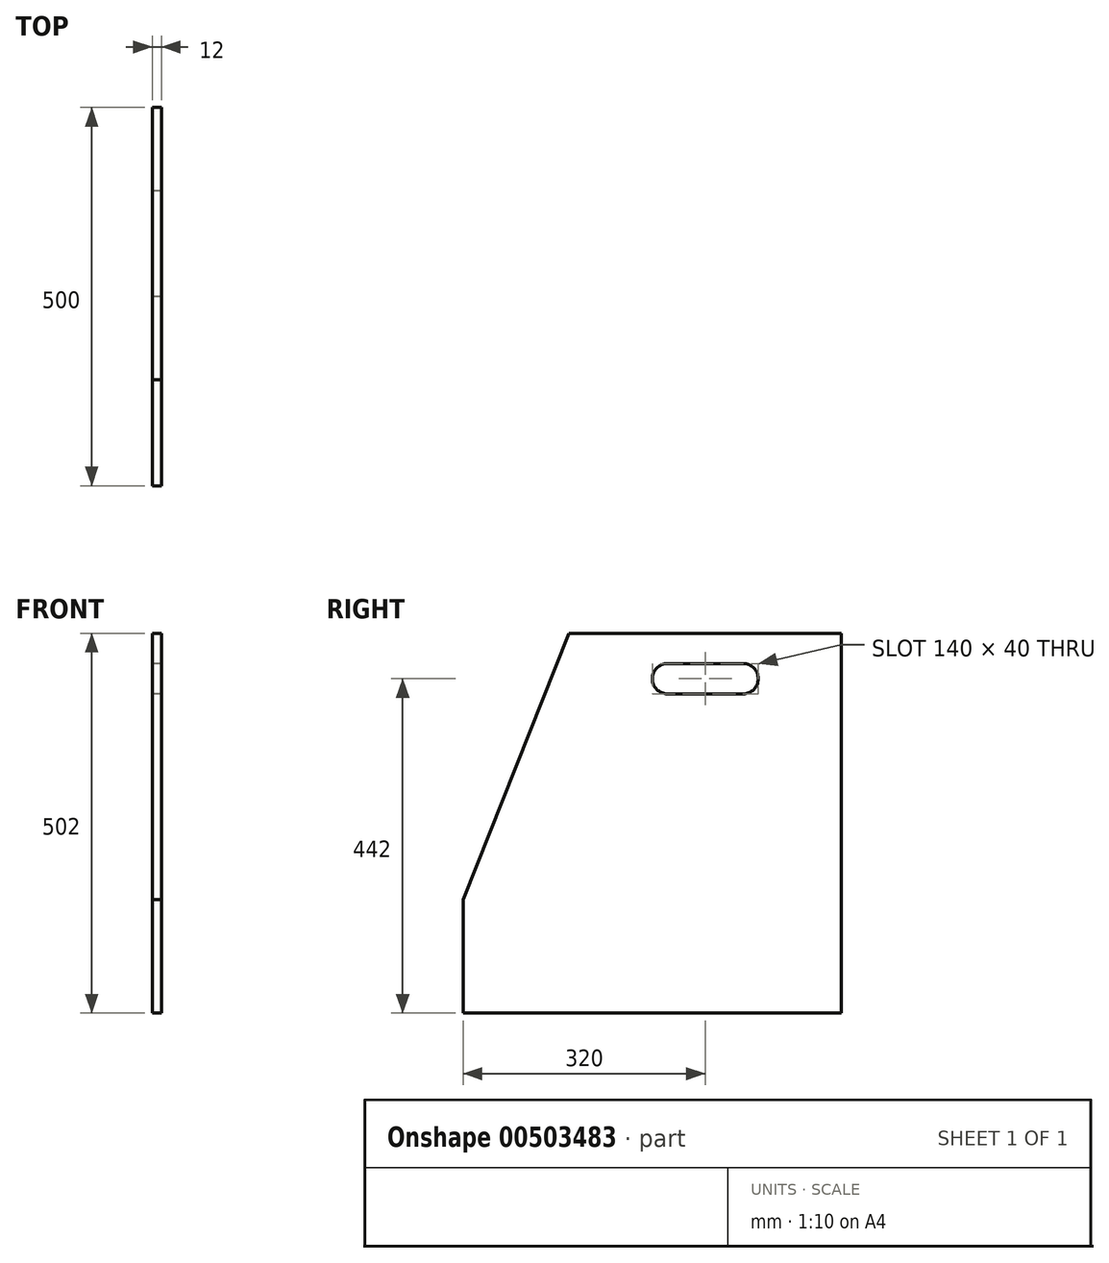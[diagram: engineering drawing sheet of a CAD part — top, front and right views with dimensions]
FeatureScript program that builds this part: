
annotation { "Feature Type Name" : "Feature", "Feature Type Description" : "" }
export const myFeature = defineFeature(function(context is Context, id is Id, definition is map)
    precondition{}
    {
        {
            var Q0;
            Q0=qCreatedBy(makeId("Top.planeOp"),FACE);
            var sketch = newSketch(context, id + "F0", { "sketchPlane" : qUnion([Q0])});
            skLineSegment(sketch, "E0.bottom", {"start": v(250, -250) * mm, "end": v(-250, -250) * mm});
            skLineSegment(sketch, "E0.top", {"start": v(250, 250) * mm, "end": v(-250, 250) * mm});
            skLineSegment(sketch, "E0.left", {"start": v(250, -250) * mm, "end": v(250, 250) * mm});
            skLineSegment(sketch, "E0.right", {"start": v(-250, -250) * mm, "end": v(-250, 250) * mm});
            skPoint(sketch, "E0.middle", {"position": v(0, 0) * mm});
            skSolve(sketch);
        }
        {
            var Q0;
            Q0=qSketchRegion(id+"F0",true);
            extrude(context, id + "F1", {"entities" : qUnion([Q0]), "depth" : 12 * mm, "offsetDistance" : 25 * mm});
        }
        {
            var Q0;
            Q0=qCreatedBy(makeId("Right.planeOp"),FACE);
            var sketch = newSketch(context, id + "F2", { "sketchPlane" : qUnion([Q0])});
            skLineSegment(sketch, "E1.bottom", {"start": v(250, -25) * mm, "end": v(-250, -25) * mm});
            skLineSegment(sketch, "E1.top", {"start": v(250, 25) * mm, "end": v(-250, 25) * mm});
            skLineSegment(sketch, "E1.left", {"start": v(250, -25) * mm, "end": v(250, 25) * mm});
            skLineSegment(sketch, "E1.right", {"start": v(-250, -25) * mm, "end": v(-250, 25) * mm});
            skPoint(sketch, "E1.middle", {"position": v(0, 0) * mm});
            skSolve(sketch);
        }
        {
            var Q0;
            Q0=qSketchRegion(id+"F2",true);
            extrude(context, id + "F3", {"entities" : qUnion([Q0]), "endBound" : BoundingType.SYMMETRIC, "depth" : 12 * mm, "offsetDistance" : 25 * mm});
        }
        {
            var Q0;
            Q0=makeQuery(id+"F3.opExtrude","SWEPT_BODY",BODY,{"disambiguationData":[OSD([sQuery(id+"F2.wireOp",EDGE,"E1.bottom"),sQuery(id+"F2.wireOp",EDGE,"E1.top"),sQuery(id+"F2.wireOp",EDGE,"E1.left"),sQuery(id+"F2.wireOp",EDGE,"E1.right")])]});
            transform(context, id + "F4", {"entities" : qUnion([Q0]), "transformType" : TransformType.TRANSLATION_3D, "dx" : 0 * mm, "dy" : 0 * mm, "dz" : -25 * mm, "makeCopy" : false});
        }
        {
            var Q0;
            Q0=qCreatedBy(makeId("Front.planeOp"),FACE);
            var sketch = newSketch(context, id + "F5", { "sketchPlane" : qUnion([Q0])});
            skLineSegment(sketch, "E2.bottom", {"start": v(250, -25) * mm, "end": v(-250, -25) * mm});
            skLineSegment(sketch, "E2.left", {"start": v(250, -25) * mm, "end": v(250, 25) * mm});
            skLineSegment(sketch, "E2.right", {"start": v(-250, -25) * mm, "end": v(-250, 25) * mm});
            skPoint(sketch, "E2.middle", {"position": v(0, 0) * mm});
            skLineSegment(sketch, "E3", {"start": v(-250, 25) * mm, "end": v(-6, 25) * mm});
            skLineSegment(sketch, "E4", {"start": v(-6, 25) * mm, "end": v(-6, 0) * mm});
            skLineSegment(sketch, "E5", {"start": v(-6, 0) * mm, "end": v(6, 0) * mm});
            skLineSegment(sketch, "E6", {"start": v(6, 0) * mm, "end": v(6, 25) * mm});
            skLineSegment(sketch, "E7", {"start": v(6, 25) * mm, "end": v(250, 25) * mm});
            skSolve(sketch);
        }
        {
            var Q0;
            Q0=qSketchRegion(id+"F5",true);
            extrude(context, id + "F6", {"entities" : qUnion([Q0]), "endBound" : BoundingType.SYMMETRIC, "depth" : 12 * mm, "offsetDistance" : 25 * mm});
        }
        {
            var Q0;
            Q0=makeQuery(id+"F6.opExtrude","SWEPT_BODY",BODY,{"disambiguationData":[OSD([sQuery(id+"F5.wireOp",EDGE,"E2.bottom"),sQuery(id+"F5.wireOp",EDGE,"E2.top"),sQuery(id+"F5.wireOp",EDGE,"E2.left"),sQuery(id+"F5.wireOp",EDGE,"E2.right")])]});
            transform(context, id + "F7", {"entities" : qUnion([Q0]), "transformType" : TransformType.TRANSLATION_3D, "dx" : 0 * mm, "dy" : 80 * mm, "dz" : -25 * mm, "makeCopy" : false});
        }
        {
            var Q0;
            Q0=makeQuery(id+"F6.opExtrude","SWEPT_BODY",BODY,{"disambiguationData":[OSD([sQuery(id+"F5.wireOp",EDGE,"E2.bottom"),sQuery(id+"F5.wireOp",EDGE,"E2.top"),sQuery(id+"F5.wireOp",EDGE,"E2.left"),sQuery(id+"F5.wireOp",EDGE,"E2.right")])]});
            transform(context, id + "F8", {"entities" : qUnion([Q0]), "transformType" : TransformType.COPY});
        }
        {
            var Q0;
            Q0=makeQuery(id+"F8.opPattern","COPY",BODY,{"derivedFrom":makeQuery(id+"F6.opExtrude","SWEPT_BODY",BODY,{"disambiguationData":[OSD([sQuery(id+"F5.wireOp",EDGE,"E2.bottom"),sQuery(id+"F5.wireOp",EDGE,"E2.top"),sQuery(id+"F5.wireOp",EDGE,"E2.left"),sQuery(id+"F5.wireOp",EDGE,"E2.right")])]}),"instanceName":"1"});
            deleteBodies(context, id + "F9", {"entities" : qUnion([Q0])});
        }
        {
            var Q0;
            Q0=makeQuery(id+"F6.opExtrude","SWEPT_BODY",BODY,{"disambiguationData":[OSD([sQuery(id+"F5.wireOp",EDGE,"E2.bottom"),sQuery(id+"F5.wireOp",EDGE,"E2.left"),sQuery(id+"F5.wireOp",EDGE,"E2.right"),sQuery(id+"F5.wireOp",EDGE,"E3"),sQuery(id+"F5.wireOp",EDGE,"E4"),sQuery(id+"F5.wireOp",EDGE,"E5"),sQuery(id+"F5.wireOp",EDGE,"E6"),sQuery(id+"F5.wireOp",EDGE,"E7")])]});
            var Q1;
            Q1=makeQuery(id+"F3.opExtrude","SWEPT_BODY",BODY,{"disambiguationData":[OSD([sQuery(id+"F2.wireOp",EDGE,"E1.bottom"),sQuery(id+"F2.wireOp",EDGE,"E1.top"),sQuery(id+"F2.wireOp",EDGE,"E1.left"),sQuery(id+"F2.wireOp",EDGE,"E1.right")])]});
            booleanBodies(context, id + "F10", {"operationType" : BooleanOperationType.SUBTRACTION, "tools" : qUnion([Q0]), "targets" : qUnion([Q1]), "keepTools" : true});
        }
        {
            var Q0;
            Q0=makeQuery(id+"F6.opExtrude","SWEPT_BODY",BODY,{"disambiguationData":[OSD([sQuery(id+"F5.wireOp",EDGE,"E2.bottom"),sQuery(id+"F5.wireOp",EDGE,"E2.left"),sQuery(id+"F5.wireOp",EDGE,"E2.right"),sQuery(id+"F5.wireOp",EDGE,"E3"),sQuery(id+"F5.wireOp",EDGE,"E4"),sQuery(id+"F5.wireOp",EDGE,"E5"),sQuery(id+"F5.wireOp",EDGE,"E6"),sQuery(id+"F5.wireOp",EDGE,"E7")])]});
            transform(context, id + "F11", {"entities" : qUnion([Q0]), "transformType" : TransformType.TRANSLATION_3D, "dx" : 0 * mm, "dy" : 164 * mm, "dz" : 0 * mm, "makeCopy" : true});
        }
        {
            var Q0;
            Q0=makeQuery(id+"F11.opPattern","COPY",BODY,{"derivedFrom":makeQuery(id+"F6.opExtrude","SWEPT_BODY",BODY,{"disambiguationData":[OSD([sQuery(id+"F5.wireOp",EDGE,"E2.bottom"),sQuery(id+"F5.wireOp",EDGE,"E2.left"),sQuery(id+"F5.wireOp",EDGE,"E2.right"),sQuery(id+"F5.wireOp",EDGE,"E3"),sQuery(id+"F5.wireOp",EDGE,"E4"),sQuery(id+"F5.wireOp",EDGE,"E5"),sQuery(id+"F5.wireOp",EDGE,"E6"),sQuery(id+"F5.wireOp",EDGE,"E7")])]}),"instanceName":"1"});
            var Q1;
            Q1=makeQuery(id+"F3.opExtrude","SWEPT_BODY",BODY,{"disambiguationData":[OSD([sQuery(id+"F2.wireOp",EDGE,"E1.bottom"),sQuery(id+"F2.wireOp",EDGE,"E1.top"),sQuery(id+"F2.wireOp",EDGE,"E1.left"),sQuery(id+"F2.wireOp",EDGE,"E1.right")])]});
            booleanBodies(context, id + "F12", {"operationType" : BooleanOperationType.SUBTRACTION, "tools" : qUnion([Q0]), "targets" : qUnion([Q1]), "keepTools" : true});
        }
        {
            var Q0;
            Q0=qCreatedBy(makeId("Right.planeOp"),FACE);
            var sketch = newSketch(context, id + "F13", { "sketchPlane" : qUnion([Q0])});
            skLineSegment(sketch, "E8", {"start": v(0, 0) * mm, "end": v(250, 0) * mm});
            skLineSegment(sketch, "E9", {"start": v(250, 0) * mm, "end": v(250, -50) * mm});
            skLineSegment(sketch, "E10", {"start": v(250, -50) * mm, "end": v(-250, -50) * mm});
            skLineSegment(sketch, "E11", {"start": v(-250, -50) * mm, "end": v(-250, 100) * mm});
            skLineSegment(sketch, "E12", {"start": v(250, 0) * mm, "end": v(250, 452) * mm});
            skLineSegment(sketch, "E13", {"start": v(250, 452) * mm, "end": v(-110, 452) * mm});
            skLineSegment(sketch, "E14", {"start": v(-110, 452) * mm, "end": v(-250, 100) * mm});
            skLineSegment(sketch, "E15", {"start": v(250, 452) * mm, "end": v(70, 452) * mm});
            skLineSegment(sketch, "E16", {"start": v(70, 452) * mm, "end": v(70, 392) * mm});
            skLineSegment(sketch, "E17.bottom", {"start": v(140, 372) * mm, "end": v(0, 372) * mm});
            skLineSegment(sketch, "E17.top", {"start": v(140, 412) * mm, "end": v(0, 412) * mm});
            skLineSegment(sketch, "E17.left", {"start": v(140, 372) * mm, "end": v(140, 412) * mm});
            skLineSegment(sketch, "E17.right", {"start": v(0, 372) * mm, "end": v(0, 412) * mm});
            skPoint(sketch, "E17.middle", {"position": v(70, 392) * mm});
            skSolve(sketch);
        }
        {
            var Q0;
            Q0=makeQuery(id+"F13.imprint","IMPRINT",FACE,{"disambiguationData":[TD([[makeQuery(id+"F13.imprint","IMPRINT",EDGE,{"derivedFrom":sQuery(id+"F13.wireOp",EDGE,"E9")}),-1.0]])]});
            extrude(context, id + "F14", {"entities" : qUnion([Q0]), "endBound" : BoundingType.SYMMETRIC, "depth" : 12 * mm, "offsetDistance" : 25 * mm});
        }
        {
            var Q0;
            Q0=makeQuery(id+"F14.opExtrude","SWEPT_EDGE",EDGE,{"disambiguationData":[OSD([sQuery(id+"F13.wireOp",EDGE,"E17.bottom"),sQuery(id+"F13.wireOp",EDGE,"E17.left")])]});
            var Q1;
            Q1=makeQuery(id+"F14.opExtrude","SWEPT_EDGE",EDGE,{"disambiguationData":[OSD([sQuery(id+"F13.wireOp",EDGE,"E17.top"),sQuery(id+"F13.wireOp",EDGE,"E17.left")])]});
            var Q2;
            Q2=makeQuery(id+"F14.opExtrude","SWEPT_EDGE",EDGE,{"disambiguationData":[OSD([sQuery(id+"F13.wireOp",EDGE,"E17.top"),sQuery(id+"F13.wireOp",EDGE,"E17.right")])]});
            var Q3;
            Q3=makeQuery(id+"F14.opExtrude","SWEPT_EDGE",EDGE,{"disambiguationData":[OSD([sQuery(id+"F13.wireOp",EDGE,"E17.bottom"),sQuery(id+"F13.wireOp",EDGE,"E17.right")])]});
            fillet(context, id + "F15", {"entities" : qUnion([Q0, Q1, Q2, Q3]), "radius" : 20 * mm, "tangentPropagation" : true, "allowEdgeOverflow" : false});
        }
        {
            var Q0;
            Q0=makeQuery(id+"F14.opExtrude","SWEPT_BODY",BODY,{"disambiguationData":[OSD([sQuery(id+"F13.wireOp",EDGE,"E9"),sQuery(id+"F13.wireOp",EDGE,"E10"),sQuery(id+"F13.wireOp",EDGE,"E11"),sQuery(id+"F13.wireOp",EDGE,"E12"),sQuery(id+"F13.wireOp",EDGE,"E13"),sQuery(id+"F13.wireOp",EDGE,"E14"),sQuery(id+"F13.wireOp",EDGE,"E17.bottom"),sQuery(id+"F13.wireOp",EDGE,"E17.top"),sQuery(id+"F13.wireOp",EDGE,"E17.left"),sQuery(id+"F13.wireOp",EDGE,"E17.right")])]});
            transform(context, id + "F16", {"entities" : qUnion([Q0]), "transformType" : TransformType.TRANSLATION_3D, "dx" : -256 * mm, "dy" : 0 * mm, "dz" : 0 * mm, "makeCopy" : false});
        }
        {
            var Q0;
            Q0=makeQuery(id+"F14.opExtrude","SWEPT_BODY",BODY,{"disambiguationData":[OSD([sQuery(id+"F13.wireOp",EDGE,"E9"),sQuery(id+"F13.wireOp",EDGE,"E10"),sQuery(id+"F13.wireOp",EDGE,"E11"),sQuery(id+"F13.wireOp",EDGE,"E12"),sQuery(id+"F13.wireOp",EDGE,"E13"),sQuery(id+"F13.wireOp",EDGE,"E14"),sQuery(id+"F13.wireOp",EDGE,"E17.bottom"),sQuery(id+"F13.wireOp",EDGE,"E17.top"),sQuery(id+"F13.wireOp",EDGE,"E17.left"),sQuery(id+"F13.wireOp",EDGE,"E17.right")])]});
            transform(context, id + "F17", {"entities" : qUnion([Q0]), "transformType" : TransformType.TRANSLATION_3D, "dx" : 512 * mm, "dy" : 0 * mm, "dz" : 0 * mm, "makeCopy" : true});
        }
        {
            var Q0;
            Q0=qCreatedBy(makeId("Front.planeOp"),FACE);
            var sketch = newSketch(context, id + "F18", { "sketchPlane" : qUnion([Q0])});
            skLineSegment(sketch, "E18", {"start": v(0, 0) * mm, "end": v(-262, 0) * mm});
            skLineSegment(sketch, "E19", {"start": v(-262, 0) * mm, "end": v(-262, -50) * mm});
            skLineSegment(sketch, "E20", {"start": v(-262, -50) * mm, "end": v(262, -50) * mm});
            skLineSegment(sketch, "E21", {"start": v(262, -50) * mm, "end": v(262, 452) * mm});
            skLineSegment(sketch, "E22", {"start": v(262, 452) * mm, "end": v(-262, 452) * mm});
            skLineSegment(sketch, "E23", {"start": v(-262, 452) * mm, "end": v(-262, 0) * mm});
            skSolve(sketch);
        }
        {
            var Q0;
            Q0=qSketchRegion(id+"F18",true);
            extrude(context, id + "F19", {"entities" : qUnion([Q0]), "endBound" : BoundingType.SYMMETRIC, "depth" : 12 * mm, "offsetDistance" : 25 * mm});
        }
        {
            var Q0;
            Q0=makeQuery(id+"F19.opExtrude","SWEPT_BODY",BODY,{"disambiguationData":[OSD([sQuery(id+"F18.wireOp",EDGE,"E19"),sQuery(id+"F18.wireOp",EDGE,"E20"),sQuery(id+"F18.wireOp",EDGE,"E21"),sQuery(id+"F18.wireOp",EDGE,"E22"),sQuery(id+"F18.wireOp",EDGE,"E23")])]});
            transform(context, id + "F20", {"entities" : qUnion([Q0]), "transformType" : TransformType.TRANSLATION_3D, "dx" : 0 * mm, "dy" : 256 * mm, "dz" : 0 * mm, "makeCopy" : false});
        }
        {
            var Q0;
            Q0=makeQuery(id+"F1.opExtrude","CAP_FACE",FACE,{"disambiguationData":[OSD([sQuery(id+"F0.wireOp",EDGE,"E0.bottom"),sQuery(id+"F0.wireOp",EDGE,"E0.top"),sQuery(id+"F0.wireOp",EDGE,"E0.left"),sQuery(id+"F0.wireOp",EDGE,"E0.right")])],"isStart":false});
            var sketch = newSketch(context, id + "F21", { "sketchPlane" : qUnion([Q0])});
            skLineSegment(sketch, "E24", {"start": v(0, 0) * mm, "end": v(0, 262) * mm});
            skLineSegment(sketch, "E25", {"start": v(0, 262) * mm, "end": v(262, 262) * mm});
            skLineSegment(sketch, "E26", {"start": v(262, 262) * mm, "end": v(262, -110) * mm});
            skLineSegment(sketch, "E27", {"start": v(262, -110) * mm, "end": v(-262, -110) * mm});
            skLineSegment(sketch, "E28", {"start": v(-262, -110) * mm, "end": v(-262, 262) * mm});
            skLineSegment(sketch, "E29", {"start": v(-262, 262) * mm, "end": v(0, 262) * mm});
            skSolve(sketch);
        }
        {
            var Q0;
            Q0=qSketchRegion(id+"F21",true);
            extrude(context, id + "F22", {"entities" : qUnion([Q0]), "depth" : 12 * mm, "offsetDistance" : 25 * mm});
        }
        {
            var Q0;
            Q0=makeQuery(id+"F22.opExtrude","SWEPT_BODY",BODY,{"disambiguationData":[OSD([sQuery(id+"F21.wireOp",EDGE,"E25"),sQuery(id+"F21.wireOp",EDGE,"E26"),sQuery(id+"F21.wireOp",EDGE,"E27"),sQuery(id+"F21.wireOp",EDGE,"E28"),sQuery(id+"F21.wireOp",EDGE,"E29")])]});
            transform(context, id + "F23", {"entities" : qUnion([Q0]), "transformType" : TransformType.TRANSLATION_3D, "dx" : 0 * mm, "dy" : 0 * mm, "dz" : 440 * mm, "makeCopy" : false});
        }
        {
            var Q0;
            Q0=qCreatedBy(makeId("Front.planeOp"),FACE);
            var sketch = newSketch(context, id + "F24", { "sketchPlane" : qUnion([Q0])});
            skLineSegment(sketch, "E30", {"start": v(0, 0) * mm, "end": v(0, 12) * mm});
            skLineSegment(sketch, "E31", {"start": v(0, 12) * mm, "end": v(250, 12) * mm});
            skLineSegment(sketch, "E32", {"start": v(250, 12) * mm, "end": v(250, 100) * mm});
            skLineSegment(sketch, "E33", {"start": v(250, 100) * mm, "end": v(-250, 100) * mm});
            skLineSegment(sketch, "E34", {"start": v(-250, 100) * mm, "end": v(-250, 12) * mm});
            skLineSegment(sketch, "E35", {"start": v(-250, 12) * mm, "end": v(0, 12) * mm});
            skSolve(sketch);
        }
        {
            var Q0;
            Q0=qSketchRegion(id+"F24",true);
            extrude(context, id + "F25", {"entities" : qUnion([Q0]), "endBound" : BoundingType.SYMMETRIC, "depth" : 12 * mm, "offsetDistance" : 25 * mm});
        }
        {
            var Q0;
            Q0=makeQuery(id+"F25.opExtrude","SWEPT_BODY",BODY,{"disambiguationData":[OSD([sQuery(id+"F24.wireOp",EDGE,"E31"),sQuery(id+"F24.wireOp",EDGE,"E32"),sQuery(id+"F24.wireOp",EDGE,"E33"),sQuery(id+"F24.wireOp",EDGE,"E34"),sQuery(id+"F24.wireOp",EDGE,"E35")])]});
            transform(context, id + "F26", {"entities" : qUnion([Q0]), "transformType" : TransformType.TRANSLATION_3D, "dx" : 0 * mm, "dy" : -244 * mm, "dz" : 0 * mm, "makeCopy" : false});
        }
        {
            var Q0;
            Q0=qCreatedBy(makeId("Top.planeOp"),FACE);
            var sketch = newSketch(context, id + "F27", { "sketchPlane" : qUnion([Q0])});
            skLineSegment(sketch, "E36", {"start": v(0, 0) * mm, "end": v(0, 70) * mm});
            skLineSegment(sketch, "E37", {"start": v(0, 70) * mm, "end": v(-18, 70) * mm});
            skLineSegment(sketch, "E38", {"start": v(-18, 70) * mm, "end": v(-18, -250) * mm});
            skLineSegment(sketch, "E39", {"start": v(-18, -250) * mm, "end": v(-30, -250) * mm});
            skLineSegment(sketch, "E40", {"start": v(-30, -250) * mm, "end": v(-30, 70) * mm});
            skLineSegment(sketch, "E41", {"start": v(-30, 70) * mm, "end": v(-18, 70) * mm});
            skSolve(sketch);
        }
        {
            var Q0;
            Q0=qSketchRegion(id+"F27",true);
            extrude(context, id + "F28", {"entities" : qUnion([Q0]), "depth" : 44 * mm, "offsetDistance" : 25 * mm});
        }
        {
            var Q0;
            Q0=makeQuery(id+"F28.opExtrude","SWEPT_BODY",BODY,{"disambiguationData":[OSD([sQuery(id+"F27.wireOp",EDGE,"E38"),sQuery(id+"F27.wireOp",EDGE,"E39"),sQuery(id+"F27.wireOp",EDGE,"E40"),sQuery(id+"F27.wireOp",EDGE,"E41")])]});
            transform(context, id + "F29", {"entities" : qUnion([Q0]), "transformType" : TransformType.TRANSLATION_3D, "dx" : 0 * mm, "dy" : 0 * mm, "dz" : -48 * mm, "makeCopy" : false});
        }
        {
            var Q0;
            Q0=makeQuery(id+"F28.opExtrude","SWEPT_BODY",BODY,{"disambiguationData":[OSD([sQuery(id+"F27.wireOp",EDGE,"E38"),sQuery(id+"F27.wireOp",EDGE,"E39"),sQuery(id+"F27.wireOp",EDGE,"E40"),sQuery(id+"F27.wireOp",EDGE,"E41")])]});
            transform(context, id + "F30", {"entities" : qUnion([Q0]), "transformType" : TransformType.TRANSLATION_3D, "dx" : -208 * mm, "dy" : 0 * mm, "dz" : 0 * mm, "makeCopy" : true});
        }
        {
            var Q0;
            Q0=qCreatedBy(makeId("Top.planeOp"),FACE);
            var sketch = newSketch(context, id + "F31", { "sketchPlane" : qUnion([Q0])});
            skLineSegment(sketch, "E42", {"start": v(0, 0) * mm, "end": v(0, -250) * mm});
            skLineSegment(sketch, "E43", {"start": v(0, -250) * mm, "end": v(-30, -250) * mm});
            skLineSegment(sketch, "E44", {"start": v(-30, -250) * mm, "end": v(-226, -250) * mm});
            skLineSegment(sketch, "E45", {"start": v(-226, -250) * mm, "end": v(-226, -238) * mm});
            skLineSegment(sketch, "E46", {"start": v(-226, -238) * mm, "end": v(-30, -238) * mm});
            skLineSegment(sketch, "E47", {"start": v(-30, -238) * mm, "end": v(-30, -250) * mm});
            skSolve(sketch);
        }
        {
            var Q0;
            Q0=qSketchRegion(id+"F31",true);
            extrude(context, id + "F32", {"entities" : qUnion([Q0]), "depth" : -44 * mm, "offsetDistance" : 25 * mm});
        }
        {
            var Q0;
            Q0=makeQuery(id+"F32.opExtrude","SWEPT_BODY",BODY,{"disambiguationData":[OSD([sQuery(id+"F31.wireOp",EDGE,"E44"),sQuery(id+"F31.wireOp",EDGE,"E45"),sQuery(id+"F31.wireOp",EDGE,"E46"),sQuery(id+"F31.wireOp",EDGE,"E47")])]});
            transform(context, id + "F33", {"entities" : qUnion([Q0]), "transformType" : TransformType.TRANSLATION_3D, "dx" : 0 * mm, "dy" : 0 * mm, "dz" : -4 * mm, "makeCopy" : false});
        }
        {
            var Q0;
            Q0=makeQuery(id+"F32.opExtrude","SWEPT_BODY",BODY,{"disambiguationData":[OSD([sQuery(id+"F31.wireOp",EDGE,"E44"),sQuery(id+"F31.wireOp",EDGE,"E45"),sQuery(id+"F31.wireOp",EDGE,"E46"),sQuery(id+"F31.wireOp",EDGE,"E47")])]});
            transform(context, id + "F34", {"entities" : qUnion([Q0]), "transformType" : TransformType.TRANSLATION_3D, "dx" : 0 * mm, "dy" : 308 * mm, "dz" : 0 * mm, "makeCopy" : true});
        }
        {
            var Q0;
            Q0=makeQuery(id+"F32.opExtrude","SWEPT_BODY",BODY,{"disambiguationData":[OSD([sQuery(id+"F31.wireOp",EDGE,"E44"),sQuery(id+"F31.wireOp",EDGE,"E45"),sQuery(id+"F31.wireOp",EDGE,"E46"),sQuery(id+"F31.wireOp",EDGE,"E47")])]});
            var Q1;
            Q1=makeQuery(id+"F30.opPattern","COPY",BODY,{"derivedFrom":makeQuery(id+"F28.opExtrude","SWEPT_BODY",BODY,{"disambiguationData":[OSD([sQuery(id+"F27.wireOp",EDGE,"E38"),sQuery(id+"F27.wireOp",EDGE,"E39"),sQuery(id+"F27.wireOp",EDGE,"E40"),sQuery(id+"F27.wireOp",EDGE,"E41")])]}),"instanceName":"1"});
            var Q2;
            Q2=makeQuery(id+"F28.opExtrude","SWEPT_BODY",BODY,{"disambiguationData":[OSD([sQuery(id+"F27.wireOp",EDGE,"E38"),sQuery(id+"F27.wireOp",EDGE,"E39"),sQuery(id+"F27.wireOp",EDGE,"E40"),sQuery(id+"F27.wireOp",EDGE,"E41")])]});
            var Q3;
            Q3=makeQuery(id+"F34.opPattern","COPY",BODY,{"derivedFrom":makeQuery(id+"F32.opExtrude","SWEPT_BODY",BODY,{"disambiguationData":[OSD([sQuery(id+"F31.wireOp",EDGE,"E44"),sQuery(id+"F31.wireOp",EDGE,"E45"),sQuery(id+"F31.wireOp",EDGE,"E46"),sQuery(id+"F31.wireOp",EDGE,"E47")])]}),"instanceName":"1"});
            transform(context, id + "F35", {"entities" : qUnion([Q0, Q1, Q2, Q3]), "transformType" : TransformType.TRANSLATION_3D, "dx" : 256 * mm, "dy" : 0 * mm, "dz" : 0 * mm, "makeCopy" : true});
        }
        {
            var Q0;
            Q0=qCreatedBy(makeId("Top.planeOp"),FACE);
            var sketch = newSketch(context, id + "F36", { "sketchPlane" : qUnion([Q0])});
            skLineSegment(sketch, "E48", {"start": v(0, 0) * mm, "end": v(-24, 0) * mm});
            skLineSegment(sketch, "E49", {"start": v(-24, 0) * mm, "end": v(-24, -244) * mm});
            skLineSegment(sketch, "E50", {"start": v(-24, -244) * mm, "end": v(-232, -244) * mm});
            skLineSegment(sketch, "E51", {"start": v(-232, -244) * mm, "end": v(-232, 64) * mm});
            skLineSegment(sketch, "E52", {"start": v(-232, 64) * mm, "end": v(-24, 64) * mm});
            skLineSegment(sketch, "E53", {"start": v(-24, 64) * mm, "end": v(-24, 0) * mm});
            skSolve(sketch);
        }
        {
            var Q0;
            Q0=qSketchRegion(id+"F36",true);
            extrude(context, id + "F37", {"entities" : qUnion([Q0]), "depth" : 3 * mm, "offsetDistance" : 25 * mm});
        }
        {
            var Q0;
            Q0=makeQuery(id+"F37.opExtrude","SWEPT_BODY",BODY,{"disambiguationData":[OSD([sQuery(id+"F36.wireOp",EDGE,"E49"),sQuery(id+"F36.wireOp",EDGE,"E50"),sQuery(id+"F36.wireOp",EDGE,"E51"),sQuery(id+"F36.wireOp",EDGE,"E52"),sQuery(id+"F36.wireOp",EDGE,"E53")])]});
            transform(context, id + "F38", {"entities" : qUnion([Q0]), "transformType" : TransformType.TRANSLATION_3D, "dx" : 0 * mm, "dy" : 0 * mm, "dz" : -44 * mm, "makeCopy" : false});
        }
        {
            var Q0;
            Q0=makeQuery(id+"F37.opExtrude","SWEPT_BODY",BODY,{"disambiguationData":[OSD([sQuery(id+"F36.wireOp",EDGE,"E49"),sQuery(id+"F36.wireOp",EDGE,"E50"),sQuery(id+"F36.wireOp",EDGE,"E51"),sQuery(id+"F36.wireOp",EDGE,"E52"),sQuery(id+"F36.wireOp",EDGE,"E53")])]});
            transform(context, id + "F39", {"entities" : qUnion([Q0]), "transformType" : TransformType.TRANSLATION_3D, "dx" : 256 * mm, "dy" : 0 * mm, "dz" : 0 * mm, "makeCopy" : true});
        }
        {
            var Q0;
            Q0=makeQuery(id+"F37.opExtrude","SWEPT_BODY",BODY,{"disambiguationData":[OSD([sQuery(id+"F36.wireOp",EDGE,"E49"),sQuery(id+"F36.wireOp",EDGE,"E50"),sQuery(id+"F36.wireOp",EDGE,"E51"),sQuery(id+"F36.wireOp",EDGE,"E52"),sQuery(id+"F36.wireOp",EDGE,"E53")])]});
            var Q1;
            Q1=makeQuery(id+"F30.opPattern","COPY",BODY,{"derivedFrom":makeQuery(id+"F28.opExtrude","SWEPT_BODY",BODY,{"disambiguationData":[OSD([sQuery(id+"F27.wireOp",EDGE,"E38"),sQuery(id+"F27.wireOp",EDGE,"E39"),sQuery(id+"F27.wireOp",EDGE,"E40"),sQuery(id+"F27.wireOp",EDGE,"E41")])]}),"instanceName":"1"});
            var Q2;
            Q2=makeQuery(id+"F32.opExtrude","SWEPT_BODY",BODY,{"disambiguationData":[OSD([sQuery(id+"F31.wireOp",EDGE,"E44"),sQuery(id+"F31.wireOp",EDGE,"E45"),sQuery(id+"F31.wireOp",EDGE,"E46"),sQuery(id+"F31.wireOp",EDGE,"E47")])]});
            var Q3;
            Q3=makeQuery(id+"F28.opExtrude","SWEPT_BODY",BODY,{"disambiguationData":[OSD([sQuery(id+"F27.wireOp",EDGE,"E38"),sQuery(id+"F27.wireOp",EDGE,"E39"),sQuery(id+"F27.wireOp",EDGE,"E40"),sQuery(id+"F27.wireOp",EDGE,"E41")])]});
            var Q4;
            Q4=makeQuery(id+"F34.opPattern","COPY",BODY,{"derivedFrom":makeQuery(id+"F32.opExtrude","SWEPT_BODY",BODY,{"disambiguationData":[OSD([sQuery(id+"F31.wireOp",EDGE,"E44"),sQuery(id+"F31.wireOp",EDGE,"E45"),sQuery(id+"F31.wireOp",EDGE,"E46"),sQuery(id+"F31.wireOp",EDGE,"E47")])]}),"instanceName":"1"});
            booleanBodies(context, id + "F40", {"operationType" : BooleanOperationType.SUBTRACTION, "tools" : qUnion([Q0]), "targets" : qUnion([Q1, Q2, Q3, Q4]), "keepTools" : true});
        }
        {
            var Q0;
            Q0=makeQuery(id+"F39.opPattern","COPY",BODY,{"derivedFrom":makeQuery(id+"F37.opExtrude","SWEPT_BODY",BODY,{"disambiguationData":[OSD([sQuery(id+"F36.wireOp",EDGE,"E49"),sQuery(id+"F36.wireOp",EDGE,"E50"),sQuery(id+"F36.wireOp",EDGE,"E51"),sQuery(id+"F36.wireOp",EDGE,"E52"),sQuery(id+"F36.wireOp",EDGE,"E53")])]}),"instanceName":"1"});
            var Q1;
            Q1=makeQuery(id+"F35.opPattern","COPY",BODY,{"derivedFrom":makeQuery(id+"F32.opExtrude","SWEPT_BODY",BODY,{"disambiguationData":[OSD([sQuery(id+"F31.wireOp",EDGE,"E44"),sQuery(id+"F31.wireOp",EDGE,"E45"),sQuery(id+"F31.wireOp",EDGE,"E46"),sQuery(id+"F31.wireOp",EDGE,"E47")])]}),"instanceName":"1"});
            var Q2;
            Q2=makeQuery(id+"F35.opPattern","COPY",BODY,{"derivedFrom":makeQuery(id+"F28.opExtrude","SWEPT_BODY",BODY,{"disambiguationData":[OSD([sQuery(id+"F27.wireOp",EDGE,"E38"),sQuery(id+"F27.wireOp",EDGE,"E39"),sQuery(id+"F27.wireOp",EDGE,"E40"),sQuery(id+"F27.wireOp",EDGE,"E41")])]}),"instanceName":"1"});
            var Q3;
            Q3=makeQuery(id+"F35.opPattern","COPY",BODY,{"derivedFrom":makeQuery(id+"F34.opPattern","COPY",BODY,{"derivedFrom":makeQuery(id+"F32.opExtrude","SWEPT_BODY",BODY,{"disambiguationData":[OSD([sQuery(id+"F31.wireOp",EDGE,"E44"),sQuery(id+"F31.wireOp",EDGE,"E45"),sQuery(id+"F31.wireOp",EDGE,"E46"),sQuery(id+"F31.wireOp",EDGE,"E47")])]}),"instanceName":"1"}),"instanceName":"1"});
            var Q4;
            Q4=makeQuery(id+"F35.opPattern","COPY",BODY,{"derivedFrom":makeQuery(id+"F30.opPattern","COPY",BODY,{"derivedFrom":makeQuery(id+"F28.opExtrude","SWEPT_BODY",BODY,{"disambiguationData":[OSD([sQuery(id+"F27.wireOp",EDGE,"E38"),sQuery(id+"F27.wireOp",EDGE,"E39"),sQuery(id+"F27.wireOp",EDGE,"E40"),sQuery(id+"F27.wireOp",EDGE,"E41")])]}),"instanceName":"1"}),"instanceName":"1"});
            booleanBodies(context, id + "F41", {"operationType" : BooleanOperationType.SUBTRACTION, "tools" : qUnion([Q0]), "targets" : qUnion([Q1, Q2, Q3, Q4]), "keepTools" : true});
        }
        {
            var Q0;
            Q0=qCreatedBy(makeId("Front.planeOp"),FACE);
            var sketch = newSketch(context, id + "F42", { "sketchPlane" : qUnion([Q0])});
            skLineSegment(sketch, "E54", {"start": v(0, 0) * mm, "end": v(0, 12) * mm});
            skLineSegment(sketch, "E55", {"start": v(0, 12) * mm, "end": v(262, 12) * mm});
            skLineSegment(sketch, "E56", {"start": v(262, 12) * mm, "end": v(262, -50) * mm});
            skLineSegment(sketch, "E57", {"start": v(262, -50) * mm, "end": v(0, -50) * mm});
            skLineSegment(sketch, "E58", {"start": v(0, -50) * mm, "end": v(0, 0) * mm});
            skSolve(sketch);
        }
        {
            var Q0;
            Q0=qSketchRegion(id+"F42",true);
            extrude(context, id + "F43", {"entities" : qUnion([Q0]), "depth" : 12 * mm, "offsetDistance" : 25 * mm});
        }
        {
            var Q0;
            Q0=makeQuery(id+"F43.opExtrude","SWEPT_BODY",BODY,{"disambiguationData":[OSD([sQuery(id+"F42.wireOp",EDGE,"E54"),sQuery(id+"F42.wireOp",EDGE,"E55"),sQuery(id+"F42.wireOp",EDGE,"E56"),sQuery(id+"F42.wireOp",EDGE,"E57"),sQuery(id+"F42.wireOp",EDGE,"E58")])]});
            transform(context, id + "F44", {"entities" : qUnion([Q0]), "transformType" : TransformType.TRANSLATION_3D, "dx" : 0 * mm, "dy" : -250 * mm, "dz" : 0 * mm, "makeCopy" : false});
        }
        {
            var Q0;
            Q0=makeQuery(id+"F43.opExtrude","SWEPT_BODY",BODY,{"disambiguationData":[OSD([sQuery(id+"F42.wireOp",EDGE,"E54"),sQuery(id+"F42.wireOp",EDGE,"E55"),sQuery(id+"F42.wireOp",EDGE,"E56"),sQuery(id+"F42.wireOp",EDGE,"E57"),sQuery(id+"F42.wireOp",EDGE,"E58")])]});
            transform(context, id + "F45", {"entities" : qUnion([Q0]), "transformType" : TransformType.TRANSLATION_3D, "dx" : -262 * mm, "dy" : 0 * mm, "dz" : 0 * mm, "makeCopy" : true});
        }
        {
            var Q0;
            Q0=makeQuery(id+"F1.opExtrude","SWEPT_BODY",BODY,{"disambiguationData":[OSD([sQuery(id+"F0.wireOp",EDGE,"E0.bottom"),sQuery(id+"F0.wireOp",EDGE,"E0.top"),sQuery(id+"F0.wireOp",EDGE,"E0.left"),sQuery(id+"F0.wireOp",EDGE,"E0.right")])]});
            var Q1;
            Q1=makeQuery(id+"F3.opExtrude","SWEPT_BODY",BODY,{"disambiguationData":[OSD([sQuery(id+"F2.wireOp",EDGE,"E1.bottom"),sQuery(id+"F2.wireOp",EDGE,"E1.top"),sQuery(id+"F2.wireOp",EDGE,"E1.left"),sQuery(id+"F2.wireOp",EDGE,"E1.right")])]});
            var Q2;
            Q2=makeQuery(id+"F6.opExtrude","SWEPT_BODY",BODY,{"disambiguationData":[OSD([sQuery(id+"F5.wireOp",EDGE,"E2.bottom"),sQuery(id+"F5.wireOp",EDGE,"E2.left"),sQuery(id+"F5.wireOp",EDGE,"E2.right"),sQuery(id+"F5.wireOp",EDGE,"E3"),sQuery(id+"F5.wireOp",EDGE,"E4"),sQuery(id+"F5.wireOp",EDGE,"E5"),sQuery(id+"F5.wireOp",EDGE,"E6"),sQuery(id+"F5.wireOp",EDGE,"E7")])]});
            var Q3;
            Q3=makeQuery(id+"F11.opPattern","COPY",BODY,{"derivedFrom":makeQuery(id+"F6.opExtrude","SWEPT_BODY",BODY,{"disambiguationData":[OSD([sQuery(id+"F5.wireOp",EDGE,"E2.bottom"),sQuery(id+"F5.wireOp",EDGE,"E2.left"),sQuery(id+"F5.wireOp",EDGE,"E2.right"),sQuery(id+"F5.wireOp",EDGE,"E3"),sQuery(id+"F5.wireOp",EDGE,"E4"),sQuery(id+"F5.wireOp",EDGE,"E5"),sQuery(id+"F5.wireOp",EDGE,"E6"),sQuery(id+"F5.wireOp",EDGE,"E7")])]}),"instanceName":"1"});
            var Q4;
            Q4=makeQuery(id+"F17.opPattern","COPY",BODY,{"derivedFrom":makeQuery(id+"F14.opExtrude","SWEPT_BODY",BODY,{"disambiguationData":[OSD([sQuery(id+"F13.wireOp",EDGE,"E9"),sQuery(id+"F13.wireOp",EDGE,"E10"),sQuery(id+"F13.wireOp",EDGE,"E11"),sQuery(id+"F13.wireOp",EDGE,"E12"),sQuery(id+"F13.wireOp",EDGE,"E13"),sQuery(id+"F13.wireOp",EDGE,"E14"),sQuery(id+"F13.wireOp",EDGE,"E17.bottom"),sQuery(id+"F13.wireOp",EDGE,"E17.top"),sQuery(id+"F13.wireOp",EDGE,"E17.left"),sQuery(id+"F13.wireOp",EDGE,"E17.right")])]}),"instanceName":"1"});
            var Q5;
            Q5=makeQuery(id+"F19.opExtrude","SWEPT_BODY",BODY,{"disambiguationData":[OSD([sQuery(id+"F18.wireOp",EDGE,"E19"),sQuery(id+"F18.wireOp",EDGE,"E20"),sQuery(id+"F18.wireOp",EDGE,"E21"),sQuery(id+"F18.wireOp",EDGE,"E22"),sQuery(id+"F18.wireOp",EDGE,"E23")])]});
            var Q6;
            Q6=makeQuery(id+"F22.opExtrude","SWEPT_BODY",BODY,{"disambiguationData":[OSD([sQuery(id+"F21.wireOp",EDGE,"E25"),sQuery(id+"F21.wireOp",EDGE,"E26"),sQuery(id+"F21.wireOp",EDGE,"E27"),sQuery(id+"F21.wireOp",EDGE,"E28"),sQuery(id+"F21.wireOp",EDGE,"E29")])]});
            deleteBodies(context, id + "F46", {"entities" : qUnion([Q0, Q1, Q2, Q3, Q4, Q5, Q6])});
        }
        {
            var Q0;
            Q0=makeQuery(id+"F25.opExtrude","SWEPT_BODY",BODY,{"disambiguationData":[OSD([sQuery(id+"F24.wireOp",EDGE,"E31"),sQuery(id+"F24.wireOp",EDGE,"E32"),sQuery(id+"F24.wireOp",EDGE,"E33"),sQuery(id+"F24.wireOp",EDGE,"E34"),sQuery(id+"F24.wireOp",EDGE,"E35")])]});
            var Q1;
            Q1=makeQuery(id+"F28.opExtrude","SWEPT_BODY",BODY,{"disambiguationData":[OSD([sQuery(id+"F27.wireOp",EDGE,"E38"),sQuery(id+"F27.wireOp",EDGE,"E39"),sQuery(id+"F27.wireOp",EDGE,"E40"),sQuery(id+"F27.wireOp",EDGE,"E41")])]});
            var Q2;
            Q2=makeQuery(id+"F30.opPattern","COPY",BODY,{"derivedFrom":makeQuery(id+"F28.opExtrude","SWEPT_BODY",BODY,{"disambiguationData":[OSD([sQuery(id+"F27.wireOp",EDGE,"E38"),sQuery(id+"F27.wireOp",EDGE,"E39"),sQuery(id+"F27.wireOp",EDGE,"E40"),sQuery(id+"F27.wireOp",EDGE,"E41")])]}),"instanceName":"1"});
            var Q3;
            Q3=makeQuery(id+"F32.opExtrude","SWEPT_BODY",BODY,{"disambiguationData":[OSD([sQuery(id+"F31.wireOp",EDGE,"E44"),sQuery(id+"F31.wireOp",EDGE,"E45"),sQuery(id+"F31.wireOp",EDGE,"E46"),sQuery(id+"F31.wireOp",EDGE,"E47")])]});
            var Q4;
            Q4=makeQuery(id+"F34.opPattern","COPY",BODY,{"derivedFrom":makeQuery(id+"F32.opExtrude","SWEPT_BODY",BODY,{"disambiguationData":[OSD([sQuery(id+"F31.wireOp",EDGE,"E44"),sQuery(id+"F31.wireOp",EDGE,"E45"),sQuery(id+"F31.wireOp",EDGE,"E46"),sQuery(id+"F31.wireOp",EDGE,"E47")])]}),"instanceName":"1"});
            var Q5;
            Q5=makeQuery(id+"F35.opPattern","COPY",BODY,{"derivedFrom":makeQuery(id+"F28.opExtrude","SWEPT_BODY",BODY,{"disambiguationData":[OSD([sQuery(id+"F27.wireOp",EDGE,"E38"),sQuery(id+"F27.wireOp",EDGE,"E39"),sQuery(id+"F27.wireOp",EDGE,"E40"),sQuery(id+"F27.wireOp",EDGE,"E41")])]}),"instanceName":"1"});
            var Q6;
            Q6=makeQuery(id+"F35.opPattern","COPY",BODY,{"derivedFrom":makeQuery(id+"F30.opPattern","COPY",BODY,{"derivedFrom":makeQuery(id+"F28.opExtrude","SWEPT_BODY",BODY,{"disambiguationData":[OSD([sQuery(id+"F27.wireOp",EDGE,"E38"),sQuery(id+"F27.wireOp",EDGE,"E39"),sQuery(id+"F27.wireOp",EDGE,"E40"),sQuery(id+"F27.wireOp",EDGE,"E41")])]}),"instanceName":"1"}),"instanceName":"1"});
            var Q7;
            Q7=makeQuery(id+"F35.opPattern","COPY",BODY,{"derivedFrom":makeQuery(id+"F32.opExtrude","SWEPT_BODY",BODY,{"disambiguationData":[OSD([sQuery(id+"F31.wireOp",EDGE,"E44"),sQuery(id+"F31.wireOp",EDGE,"E45"),sQuery(id+"F31.wireOp",EDGE,"E46"),sQuery(id+"F31.wireOp",EDGE,"E47")])]}),"instanceName":"1"});
            var Q8;
            Q8=makeQuery(id+"F35.opPattern","COPY",BODY,{"derivedFrom":makeQuery(id+"F34.opPattern","COPY",BODY,{"derivedFrom":makeQuery(id+"F32.opExtrude","SWEPT_BODY",BODY,{"disambiguationData":[OSD([sQuery(id+"F31.wireOp",EDGE,"E44"),sQuery(id+"F31.wireOp",EDGE,"E45"),sQuery(id+"F31.wireOp",EDGE,"E46"),sQuery(id+"F31.wireOp",EDGE,"E47")])]}),"instanceName":"1"}),"instanceName":"1"});
            var Q9;
            Q9=makeQuery(id+"F37.opExtrude","SWEPT_BODY",BODY,{"disambiguationData":[OSD([sQuery(id+"F36.wireOp",EDGE,"E49"),sQuery(id+"F36.wireOp",EDGE,"E50"),sQuery(id+"F36.wireOp",EDGE,"E51"),sQuery(id+"F36.wireOp",EDGE,"E52"),sQuery(id+"F36.wireOp",EDGE,"E53")])]});
            var Q10;
            Q10=makeQuery(id+"F39.opPattern","COPY",BODY,{"derivedFrom":makeQuery(id+"F37.opExtrude","SWEPT_BODY",BODY,{"disambiguationData":[OSD([sQuery(id+"F36.wireOp",EDGE,"E49"),sQuery(id+"F36.wireOp",EDGE,"E50"),sQuery(id+"F36.wireOp",EDGE,"E51"),sQuery(id+"F36.wireOp",EDGE,"E52"),sQuery(id+"F36.wireOp",EDGE,"E53")])]}),"instanceName":"1"});
            var Q11;
            Q11=makeQuery(id+"F43.opExtrude","SWEPT_BODY",BODY,{"disambiguationData":[OSD([sQuery(id+"F42.wireOp",EDGE,"E54"),sQuery(id+"F42.wireOp",EDGE,"E55"),sQuery(id+"F42.wireOp",EDGE,"E56"),sQuery(id+"F42.wireOp",EDGE,"E57"),sQuery(id+"F42.wireOp",EDGE,"E58")])]});
            var Q12;
            Q12=makeQuery(id+"F45.opPattern","COPY",BODY,{"derivedFrom":makeQuery(id+"F43.opExtrude","SWEPT_BODY",BODY,{"disambiguationData":[OSD([sQuery(id+"F42.wireOp",EDGE,"E54"),sQuery(id+"F42.wireOp",EDGE,"E55"),sQuery(id+"F42.wireOp",EDGE,"E56"),sQuery(id+"F42.wireOp",EDGE,"E57"),sQuery(id+"F42.wireOp",EDGE,"E58")])]}),"instanceName":"1"});
            deleteBodies(context, id + "F47", {"entities" : qUnion([Q0, Q1, Q2, Q3, Q4, Q5, Q6, Q7, Q8, Q9, Q10, Q11, Q12])});
        }
    });
